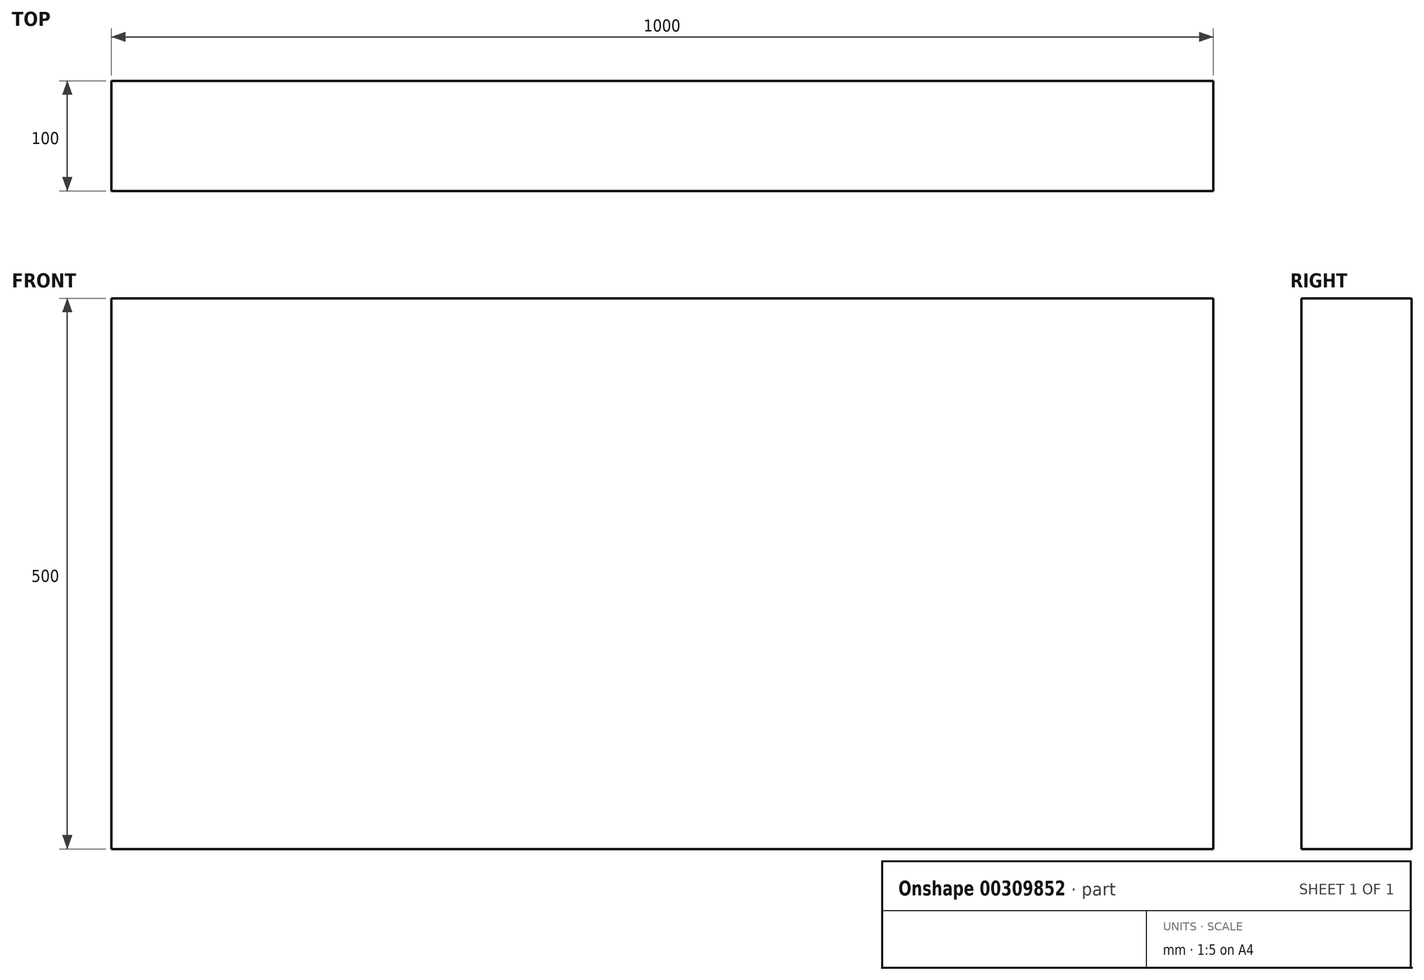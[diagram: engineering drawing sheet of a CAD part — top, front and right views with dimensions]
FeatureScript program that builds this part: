
annotation { "Feature Type Name" : "Feature", "Feature Type Description" : "" }
export const myFeature = defineFeature(function(context is Context, id is Id, definition is map)
    precondition{}
    {
        {
            var Q0;
            Q0=qCreatedBy(makeId("Front.planeOp"),FACE);
            var sketch = newSketch(context, id + "F0", { "sketchPlane" : qUnion([Q0])});
            skLineSegment(sketch, "E0.bottom", {"start": v(500, -250) * mm, "end": v(-500, -250) * mm});
            skLineSegment(sketch, "E0.top", {"start": v(500, 250) * mm, "end": v(-500, 250) * mm});
            skLineSegment(sketch, "E0.left", {"start": v(500, -250) * mm, "end": v(500, 250) * mm});
            skLineSegment(sketch, "E0.right", {"start": v(-500, -250) * mm, "end": v(-500, 250) * mm});
            skPoint(sketch, "E0.middle", {"position": v(0, 0) * mm});
            skSolve(sketch);
        }
        {
            var Q0;
            Q0=makeQuery(id+"F0.imprint","IMPRINT",FACE,{"disambiguationData":[TD([[makeQuery(id+"F0.imprint","IMPRINT",EDGE,{"derivedFrom":sQuery(id+"F0.wireOp",EDGE,"E0.bottom")}),-1.0]])]});
            extrude(context, id + "F1", {"entities" : qUnion([Q0]), "depth" : 100 * mm});
        }
    });
